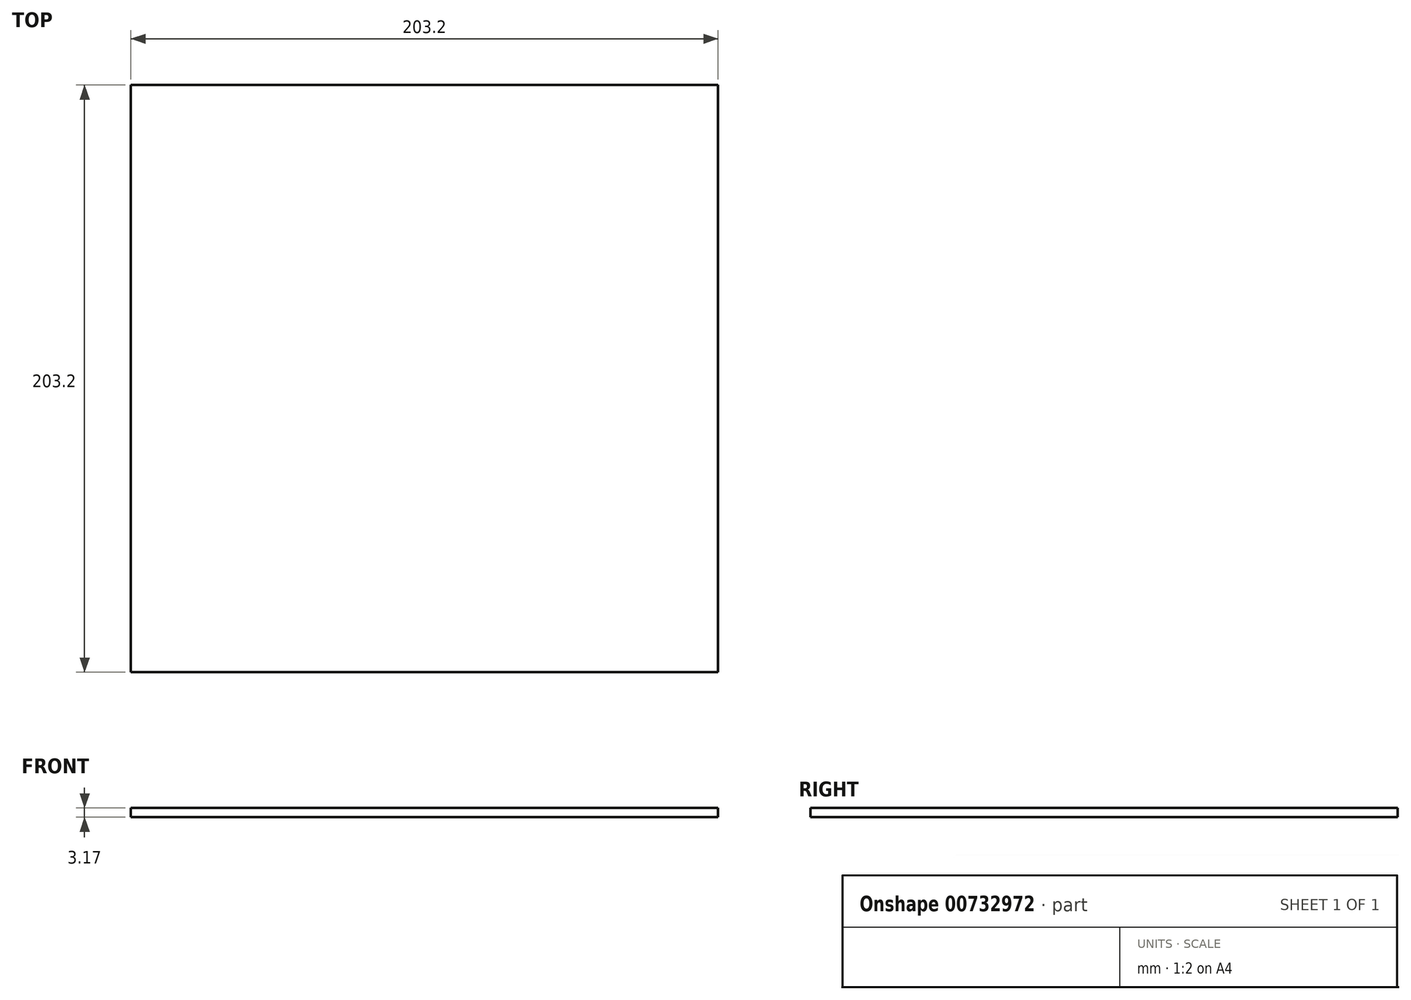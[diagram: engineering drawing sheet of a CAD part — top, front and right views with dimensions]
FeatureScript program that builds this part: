
annotation { "Feature Type Name" : "Feature", "Feature Type Description" : "" }
export const myFeature = defineFeature(function(context is Context, id is Id, definition is map)
    precondition{}
    {
        {
            var Q0;
            Q0=qCreatedBy(makeId("Top.planeOp"),FACE);
            var sketch = newSketch(context, id + "F0", { "sketchPlane" : qUnion([Q0])});
            skLineSegment(sketch, "E0.bottom", {"start": v(0, 0) * mm, "end": v(-203.2, 0) * mm});
            skLineSegment(sketch, "E0.top", {"start": v(0, 203.2) * mm, "end": v(-203.2, 203.2) * mm});
            skLineSegment(sketch, "E0.left", {"start": v(0, 0) * mm, "end": v(0, 203.2) * mm});
            skLineSegment(sketch, "E0.right", {"start": v(-203.2, 0) * mm, "end": v(-203.2, 203.2) * mm});
            skSolve(sketch);
        }
        {
            var Q0;
            Q0=makeQuery(id+"F0.imprint","IMPRINT",FACE,{"disambiguationData":[TD([[makeQuery(id+"F0.imprint","IMPRINT",EDGE,{"derivedFrom":sQuery(id+"F0.wireOp",EDGE,"E0.bottom")}),-1.0]])]});
            extrude(context, id + "F1", {"entities" : qUnion([Q0]), "depth" : 3.17 * mm, "offsetDistance" : 25.4 * mm});
        }
    });
